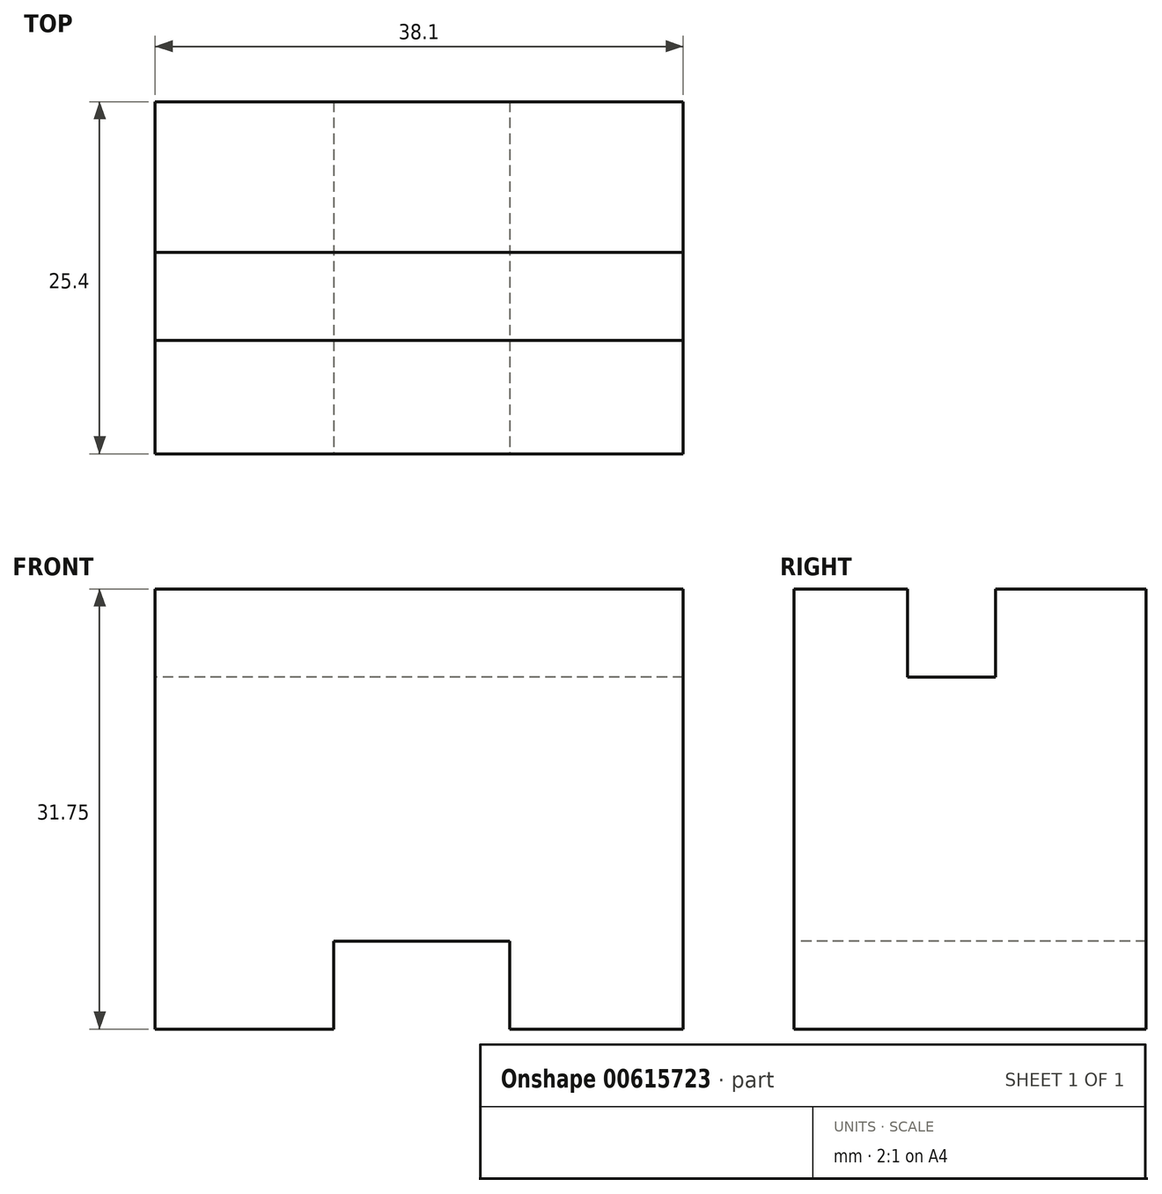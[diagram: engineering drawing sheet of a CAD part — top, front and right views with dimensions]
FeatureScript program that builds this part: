
annotation { "Feature Type Name" : "Feature", "Feature Type Description" : "" }
export const myFeature = defineFeature(function(context is Context, id is Id, definition is map)
    precondition{}
    {
        {
            var Q0;
            Q0=qCreatedBy(makeId("Front.planeOp"),FACE);
            var sketch = newSketch(context, id + "F0", { "sketchPlane" : qUnion([Q0])});
            skLineSegment(sketch, "E0", {"start": v(0, 0) * mm, "end": v(0, 31.75) * mm});
            skLineSegment(sketch, "E1", {"start": v(0, 31.75) * mm, "end": v(38.1, 31.75) * mm});
            skLineSegment(sketch, "E2", {"start": v(38.1, 31.75) * mm, "end": v(38.1, 0) * mm});
            skLineSegment(sketch, "E3", {"start": v(0, 0) * mm, "end": v(38.1, 0) * mm});
            skSolve(sketch);
        }
        {
            var Q0;
            Q0=makeQuery(id+"F0.imprint","IMPRINT",FACE,{"disambiguationData":[TD([[makeQuery(id+"F0.imprint","IMPRINT",EDGE,{"derivedFrom":sQuery(id+"F0.wireOp",EDGE,"E0")}),-1.0]])]});
            extrude(context, id + "F1", {"entities" : qUnion([Q0]), "depth" : 25.4 * mm, "offsetDistance" : 25.4 * mm});
        }
        {
            var Q0;
            Q0=makeQuery(id+"F1.opExtrude","CAP_FACE",FACE,{"disambiguationData":[OSD([sQuery(id+"F0.wireOp",EDGE,"E0"),sQuery(id+"F0.wireOp",EDGE,"E1"),sQuery(id+"F0.wireOp",EDGE,"E2"),sQuery(id+"F0.wireOp",EDGE,"E3")])],"isStart":false});
            var sketch = newSketch(context, id + "F2", { "sketchPlane" : qUnion([Q0])});
            skLineSegment(sketch, "E4", {"start": v(12.87, 0) * mm, "end": v(12.87, 6.35) * mm});
            skLineSegment(sketch, "E5", {"start": v(12.87, 6.35) * mm, "end": v(25.57, 6.35) * mm});
            skLineSegment(sketch, "E6", {"start": v(25.57, 6.35) * mm, "end": v(25.57, 0) * mm});
            skSolve(sketch);
        }
        {
            var Q0;
            {var subQ0=sQuery(id+"F2.wireOp",EDGE,"E4");Q0=makeQuery(id+"F2.imprint","IMPRINT",FACE,{"disambiguationData":[TD([[makeQuery(id+"F2.imprint","IMPRINT",EDGE,{"derivedFrom":subQ0}),-1.0]])]});}
            extrude(context, id + "F3", {"entities" : qUnion([Q0]), "operationType" : NewBodyOperationType.REMOVE, "oppositeDirection" : true, "depth" : 25.4 * mm, "offsetDistance" : 25.4 * mm});
        }
        {
            var Q0;
            Q0=makeQuery(id+"F1.opExtrude","SWEPT_FACE",FACE,{"disambiguationData":[OSD([sQuery(id+"F0.wireOp",EDGE,"E1")])]});
            var sketch = newSketch(context, id + "F4", { "sketchPlane" : qUnion([Q0])});
            skLineSegment(sketch, "E7", {"start": v(38.1, -10.86) * mm, "end": v(38.1, -17.21) * mm});
            skLineSegment(sketch, "E8", {"start": v(38.1, -10.86) * mm, "end": v(0, -10.86) * mm});
            skLineSegment(sketch, "E9", {"start": v(38.1, -17.21) * mm, "end": v(0, -17.21) * mm});
            skSolve(sketch);
        }
        {
            var Q0;
            Q0=makeQuery(id+"F4.imprint","IMPRINT",FACE,{"disambiguationData":[TD([[makeQuery(id+"F4.imprint","IMPRINT",EDGE,{"derivedFrom":sQuery(id+"F4.wireOp",EDGE,"E7")}),1.0]])]});
            extrude(context, id + "F5", {"entities" : qUnion([Q0]), "operationType" : NewBodyOperationType.REMOVE, "oppositeDirection" : true, "depth" : 6.35 * mm, "offsetDistance" : 25.4 * mm});
        }
    });
